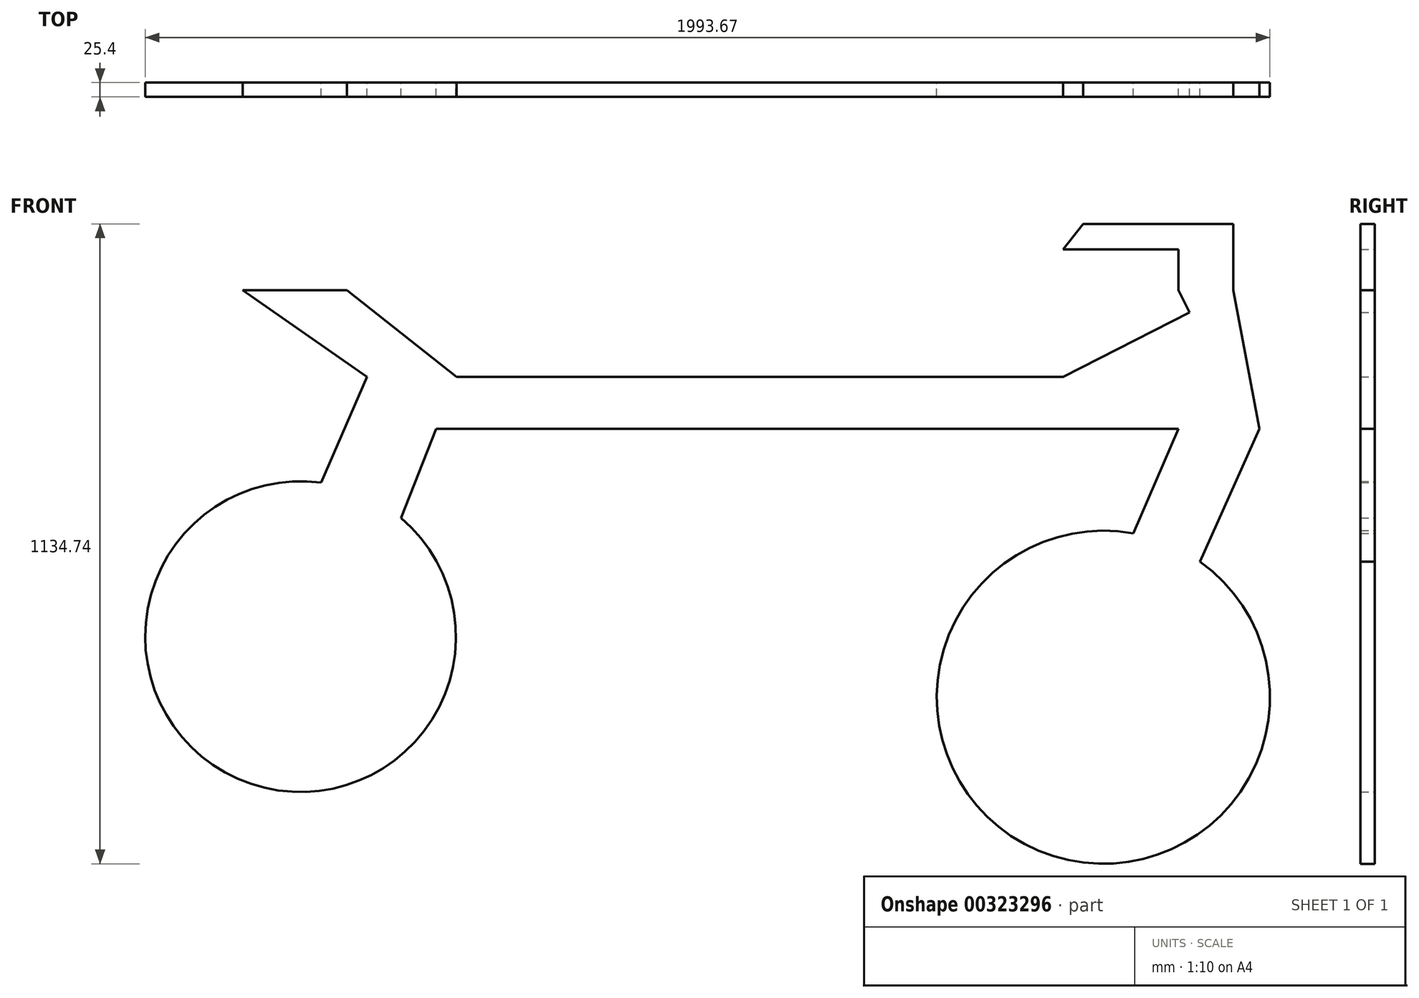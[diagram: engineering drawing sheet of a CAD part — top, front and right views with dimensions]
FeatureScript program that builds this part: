
annotation { "Feature Type Name" : "Feature", "Feature Type Description" : "" }
export const myFeature = defineFeature(function(context is Context, id is Id, definition is map)
    precondition{}
    {
        {
            var Q0;
            Q0=qCreatedBy(makeId("Front.planeOp"),FACE);
            var sketch = newSketch(context, id + "F0", { "sketchPlane" : qUnion([Q0])});
            skLineSegment(sketch, "E0", {"start": v(-1241.94, 245.68) * mm, "end": v(-1057.68, 245.68) * mm});
            skLineSegment(sketch, "E1", {"start": v(-1057.68, 245.68) * mm, "end": v(-863.18, 92.13) * mm});
            skLineSegment(sketch, "E2", {"start": v(-1241.94, 245.68) * mm, "end": v(-1021.85, 92.13) * mm});
            skLineSegment(sketch, "E3", {"start": v(-1021.85, 92.13) * mm, "end": v(-1241.94, -414.59) * mm});
            skLineSegment(sketch, "E4", {"start": v(-1241.94, -414.59) * mm, "end": v(-1088.44, -481.26) * mm});
            skLineSegment(sketch, "E5", {"start": v(-1088.44, -481.26) * mm, "end": v(-863.18, 92.13) * mm});
            skLineSegment(sketch, "E6", {"start": v(-899.37, 0) * mm, "end": v(211.68, 0) * mm});
            skLineSegment(sketch, "E7", {"start": v(-863.18, 92.13) * mm, "end": v(211.68, 92.13) * mm});
            skLineSegment(sketch, "E8", {"start": v(211.68, 92.13) * mm, "end": v(513.67, 245.68) * mm});
            skLineSegment(sketch, "E9", {"start": v(513.67, 245.68) * mm, "end": v(513.67, 363.4) * mm});
            skLineSegment(sketch, "E10", {"start": v(513.67, 363.4) * mm, "end": v(247.51, 363.4) * mm});
            skLineSegment(sketch, "E11", {"start": v(247.51, 363.4) * mm, "end": v(211.68, 318.02) * mm});
            skLineSegment(sketch, "E12", {"start": v(211.68, 318.02) * mm, "end": v(416.42, 318.02) * mm});
            skLineSegment(sketch, "E13", {"start": v(416.42, 318.02) * mm, "end": v(416.42, 245.68) * mm});
            skLineSegment(sketch, "E14", {"start": v(416.42, 245.68) * mm, "end": v(436.4, 206.4) * mm});
            skLineSegment(sketch, "E15", {"start": v(211.68, 0) * mm, "end": v(416.42, 0) * mm});
            skLineSegment(sketch, "E16", {"start": v(416.42, 0) * mm, "end": v(211.68, -476) * mm});
            skLineSegment(sketch, "E17", {"start": v(211.68, -476) * mm, "end": v(140.02, -593.73) * mm});
            skLineSegment(sketch, "E18", {"start": v(140.02, -593.73) * mm, "end": v(261.48, -667.66) * mm});
            skLineSegment(sketch, "E19", {"start": v(261.48, -667.66) * mm, "end": v(559.73, 0) * mm});
            skLineSegment(sketch, "E20", {"start": v(559.73, 0) * mm, "end": v(513.67, 245.68) * mm});
            skCircle(sketch, "E21", {"center": v(-1139.57, -368.52) * mm, "radius": 275.44 * mm});
            skCircle(sketch, "E22", {"center": v(283.34, -476) * mm, "radius": 295.32 * mm});
            skSolve(sketch);
        }
        {
            var Q0;
            Q0 = qSketchRegion(id + "F0", true);
            extrude(context, id + "F1", {"entities" : qUnion([Q0]), "endBound" : BoundingType.SYMMETRIC, "depth" : 25.4 * mm});
        }
    });
